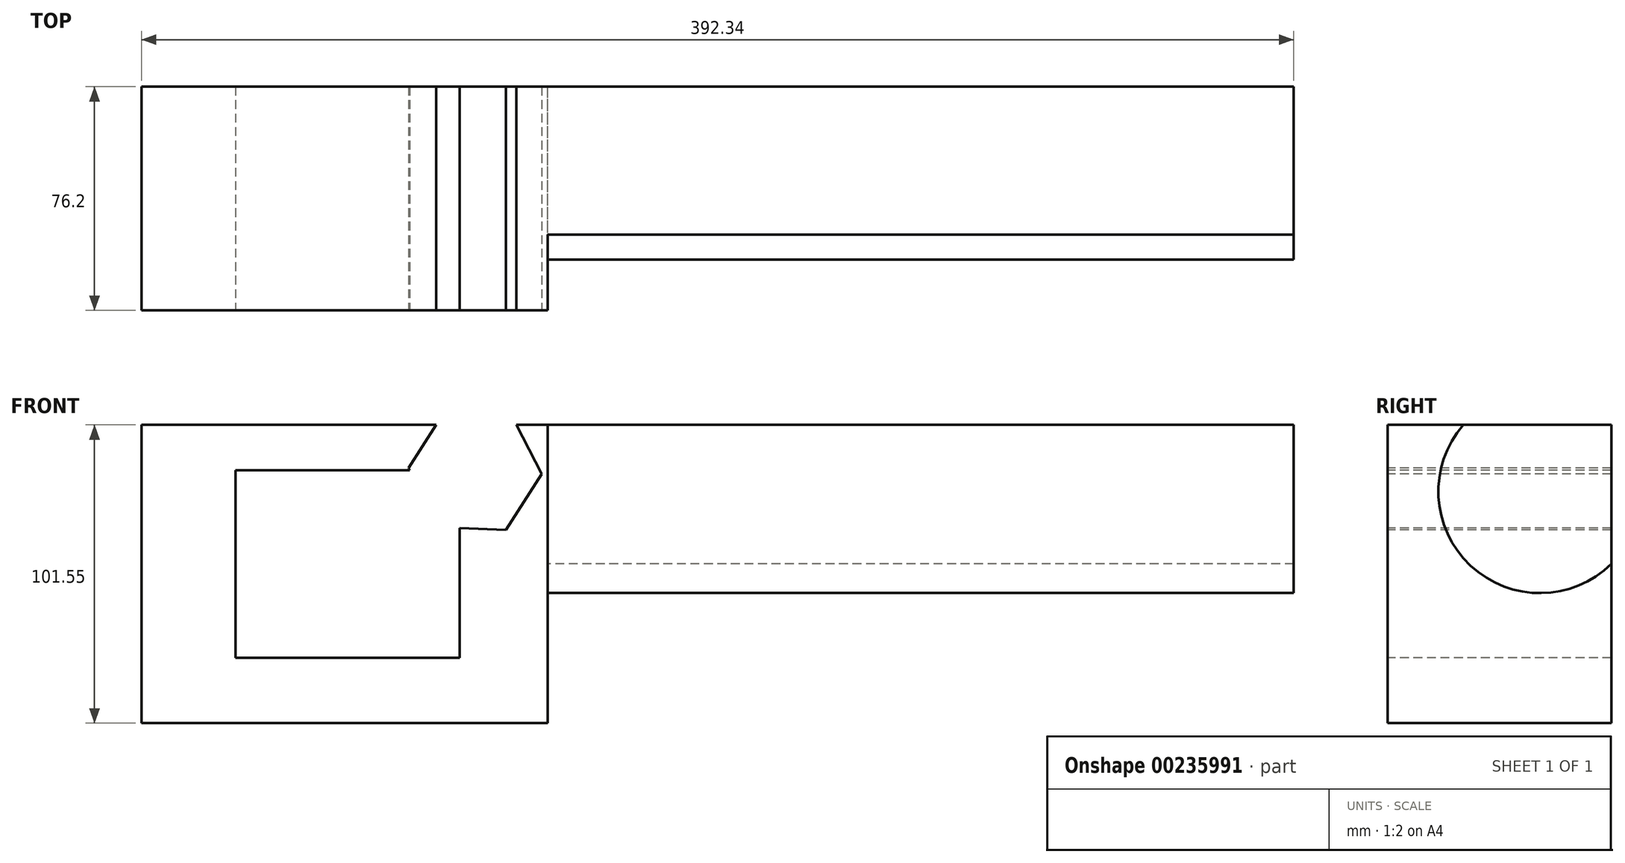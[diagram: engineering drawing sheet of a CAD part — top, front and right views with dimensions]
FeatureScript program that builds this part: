
annotation { "Feature Type Name" : "Feature", "Feature Type Description" : "" }
export const myFeature = defineFeature(function(context is Context, id is Id, definition is map)
    precondition{}
    {
        {
            var Q0;
            Q0=qCreatedBy(makeId("Front.planeOp"),FACE);
            var sketch = newSketch(context, id + "F0", { "sketchPlane" : qUnion([Q0])});
            skLineSegment(sketch, "E0.bottom", {"start": v(-68.46, 50.06) * mm, "end": v(69.88, 50.06) * mm});
            skLineSegment(sketch, "E0.top", {"start": v(-68.46, -51.49) * mm, "end": v(69.88, -51.49) * mm});
            skLineSegment(sketch, "E0.left", {"start": v(-68.46, 50.06) * mm, "end": v(-68.46, -51.49) * mm});
            skLineSegment(sketch, "E0.right", {"start": v(69.88, 50.06) * mm, "end": v(69.88, -51.49) * mm});
            skSolve(sketch);
        }
        {
            var Q0;
            Q0=makeQuery(id+"F0.imprint","IMPRINT",FACE,{"disambiguationData":[TD([[makeQuery(id+"F0.imprint","IMPRINT",EDGE,{"derivedFrom":sQuery(id+"F0.wireOp",EDGE,"E0.bottom")}),-1.0]])]});
            extrude(context, id + "F1", {"entities" : qUnion([Q0]), "depth" : 76.2 * mm});
        }
        {
            var Q0;
            Q0=makeQuery(id+"F1.opExtrude","CAP_FACE",FACE,{"disambiguationData":[OSD([sQuery(id+"F0.wireOp",EDGE,"E0.bottom"),sQuery(id+"F0.wireOp",EDGE,"E0.top"),sQuery(id+"F0.wireOp",EDGE,"E0.left"),sQuery(id+"F0.wireOp",EDGE,"E0.right")])],"isStart":false});
            var sketch = newSketch(context, id + "F2", { "sketchPlane" : qUnion([Q0])});
            skLineSegment(sketch, "E1.bottom", {"start": v(-36.4, 34.65) * mm, "end": v(39.83, 34.65) * mm});
            skLineSegment(sketch, "E1.top", {"start": v(-36.4, -29.22) * mm, "end": v(39.83, -29.22) * mm});
            skLineSegment(sketch, "E1.left", {"start": v(-36.4, 34.65) * mm, "end": v(-36.4, -29.22) * mm});
            skLineSegment(sketch, "E1.right", {"start": v(39.83, 34.65) * mm, "end": v(39.83, -29.22) * mm});
            skSolve(sketch);
        }
        {
            var Q0;
            Q0=makeQuery(id+"F2.imprint","IMPRINT",FACE,{"disambiguationData":[TD([[makeQuery(id+"F2.imprint","IMPRINT",EDGE,{"derivedFrom":sQuery(id+"F2.wireOp",EDGE,"E1.bottom")}),-1.0]])]});
            extrude(context, id + "F3", {"entities" : qUnion([Q0]), "operationType" : NewBodyOperationType.REMOVE, "oppositeDirection" : true, "depth" : 101.6 * mm});
        }
        {
            var Q0;
            Q0=makeQuery(id+"F1.opExtrude","SWEPT_FACE",FACE,{"disambiguationData":[OSD([sQuery(id+"F0.wireOp",EDGE,"E0.right")])]});
            var sketch = newSketch(context, id + "F4", { "sketchPlane" : qUnion([Q0])});
            skCircle(sketch, "E2", {"center": v(-24.33, 27.36) * mm, "radius": 34.6 * mm});
            skCircle(sketch, "E3", {"center": v(-190.04, 9.57) * mm, "radius": 21.22 * mm});
            skSolve(sketch);
        }
        {
            var Q0;
            {var subQ0=sQuery(id+"F4.wireOp",EDGE,"E2");var subQ1=sQuery(id+"F0.wireOp",EDGE,"E0.right");var subQ4=makeQuery(id+"F1.opExtrude","CAP_EDGE",EDGE,{"disambiguationData":[OSD([subQ1])],"isStart":true});var subQ5=makeQuery(id+"F4.imprint","INTERSECT",VERTEX,{"derivedFrom":[subQ4,subQ0]});Q0=makeQuery(id+"F4.imprint","IMPRINT",FACE,{"disambiguationData":[TD([[makeQuery(id+"F4.imprint","IMPRINT",EDGE,{"disambiguationData":[TD([[subQ5,1.0]])],"derivedFrom":subQ0}),1.0]])]});}
            extrude(context, id + "F5", {"entities" : qUnion([Q0]), "operationType" : NewBodyOperationType.ADD, "depth" : 254 * mm});
        }
        {
            var Q0;
            Q0=makeQuery(id+"F1.opExtrude","CAP_FACE",FACE,{"disambiguationData":[OSD([sQuery(id+"F0.wireOp",EDGE,"E0.bottom"),sQuery(id+"F0.wireOp",EDGE,"E0.top"),sQuery(id+"F0.wireOp",EDGE,"E0.left"),sQuery(id+"F0.wireOp",EDGE,"E0.right")])],"isStart":false});
            var sketch = newSketch(context, id + "F6", { "sketchPlane" : qUnion([Q0])});
            skCircle(sketch, "E4.cCircle", {"center": v(45.19, 34.37) * mm, "radius": 19.62 * mm, "construction": true});
            skLineSegment(sketch, "E4.0", {"start": v(67.82, 33.37) * mm, "end": v(55.64, 14.27) * mm});
            skLineSegment(sketch, "E4.1", {"start": v(55.64, 14.27) * mm, "end": v(33, 15.27) * mm});
            skLineSegment(sketch, "E4.2", {"start": v(33, 15.27) * mm, "end": v(22.55, 35.37) * mm});
            skLineSegment(sketch, "E4.3", {"start": v(22.55, 35.37) * mm, "end": v(34.74, 54.48) * mm});
            skLineSegment(sketch, "E4.4", {"start": v(34.74, 54.48) * mm, "end": v(57.37, 53.47) * mm});
            skLineSegment(sketch, "E4.5", {"start": v(57.37, 53.47) * mm, "end": v(67.82, 33.37) * mm});
            skPoint(sketch, "E4.0.midPoint", {"position": v(61.73, 23.82) * mm});
            skSolve(sketch);
        }
        {
            var Q0;
            {var subQ0=sQuery(id+"F6.wireOp",EDGE,"E4.4");Q0=makeQuery(id+"F6.imprint","IMPRINT",FACE,{"disambiguationData":[TD([[makeQuery(id+"F6.imprint","IMPRINT",EDGE,{"derivedFrom":subQ0}),-1.0]])]});}
            var Q1;
            {var subQ5=sQuery(id+"F6.wireOp",EDGE,"E4.0");Q1=makeQuery(id+"F6.imprint","IMPRINT",FACE,{"disambiguationData":[TD([[makeQuery(id+"F6.imprint","IMPRINT",EDGE,{"derivedFrom":subQ5}),-1.0]])]});}
            extrude(context, id + "F7", {"entities" : qUnion([Q0, Q1]), "operationType" : NewBodyOperationType.REMOVE, "oppositeDirection" : true, "depth" : 101.6 * mm});
        }
    });
